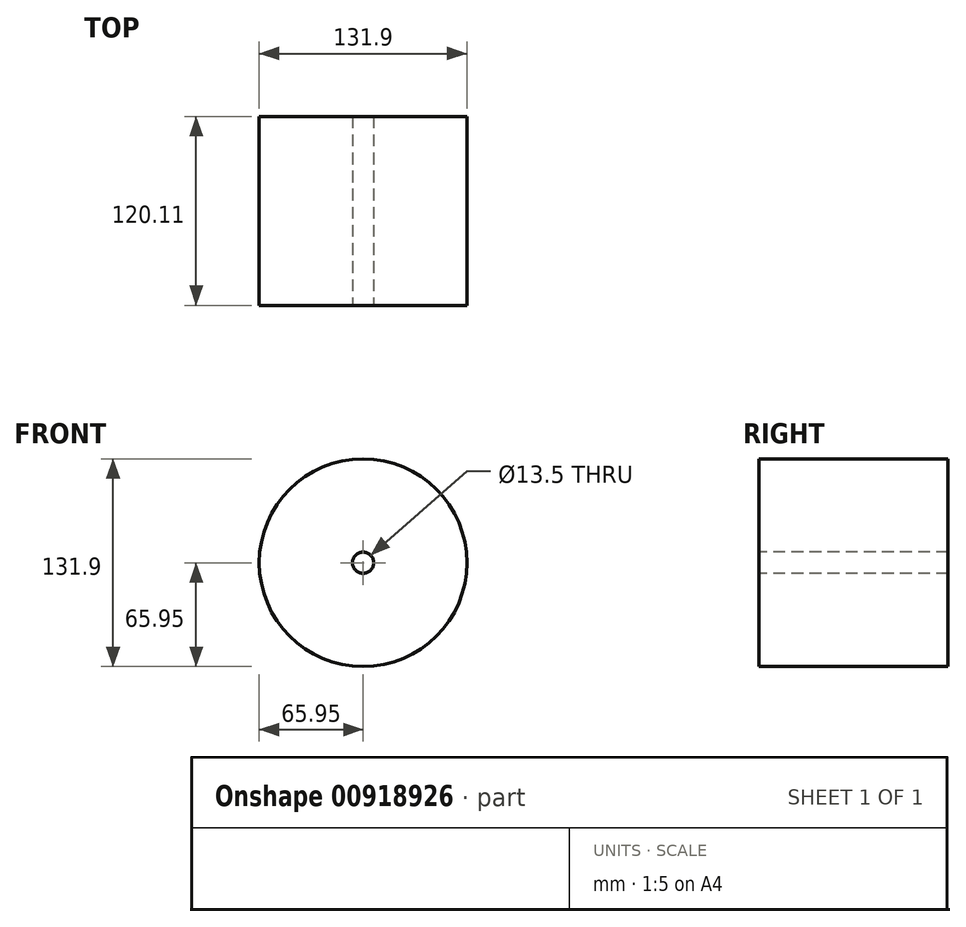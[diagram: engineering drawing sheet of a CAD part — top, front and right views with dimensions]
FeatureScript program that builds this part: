
annotation { "Feature Type Name" : "Feature", "Feature Type Description" : "" }
export const myFeature = defineFeature(function(context is Context, id is Id, definition is map)
    precondition{}
    {
        {
            var Q0;
            Q0=qCreatedBy(makeId("Right.planeOp"),FACE);
            var sketch = newSketch(context, id + "F0", { "sketchPlane" : qUnion([Q0])});
            skLineSegment(sketch, "E0.bottom", {"start": v(-120.1, 65.95) * mm, "end": v(0, 65.95) * mm});
            skLineSegment(sketch, "E0.top", {"start": v(-120.1, 0) * mm, "end": v(0, 0) * mm});
            skLineSegment(sketch, "E0.left", {"start": v(-120.1, 65.95) * mm, "end": v(-120.1, 0) * mm});
            skLineSegment(sketch, "E0.right", {"start": v(0, 65.95) * mm, "end": v(0, 0) * mm});
            skSolve(sketch);
        }
        {
            var Q0;
            Q0 = qSketchRegion(id + "F0", true);
            var Q1;
            Q1=sQuery(id+"F0.wireOp",EDGE,"E0.top");
            revolve(context, id + "F1", {"surfaceOperationType" : NewSurfaceOperationType.NEW, "entities" : qUnion([Q0]), "axis" : qUnion([Q1]), "revolveType" : RevolveType.FULL});
        }
        {
            var Q0;
            Q0=makeQuery(id+"F1.opRevolve","SWEPT_FACE",FACE,{"disambiguationData":[OSD([sQuery(id+"F0.wireOp",EDGE,"E0.left")])]});
            var sketch = newSketch(context, id + "F2", { "sketchPlane" : qUnion([Q0])});
            skCircle(sketch, "E1", {"center": v(0, 0) * mm, "radius": 28.43 * mm});
            skSolve(sketch);
        }
        {
            var Q0;
            Q0=sQuery(id+"F2.wireOp",VERTEX,"E1.center");
            var Q1;
            Q1=makeQuery(id+"F1.opRevolve","SWEPT_BODY",BODY,{"disambiguationData":[OSD([sQuery(id+"F0.wireOp",EDGE,"E0.bottom"),sQuery(id+"F0.wireOp",EDGE,"E0.top"),sQuery(id+"F0.wireOp",EDGE,"E0.left"),sQuery(id+"F0.wireOp",EDGE,"E0.right")])]});
            hole(context, id + "F3", {"style" : HoleStyle.SIMPLE, "endStyle" : HoleEndStyle.THROUGH, "standardTappedOrClearance" : lookupTablePath({ "fit" : "Normal", "standard" : "ISO", "size" : "M12", "type" : "Clearance" }), "standardBlindInLast" : lookupTablePath({ "fit" : "Normal", "standard" : "ISO", "size" : "M12", "type" : "Clearance" }), "holeDiameter" : 13.5 * mm, "majorDiameter" : 5 * mm, "isTappedThrough" : true, "tappedDepth" : 12 * mm, "tapClearance" : 3, "locations" : qUnion([Q0]), "scope" : qUnion([Q1])});
        }
    });
